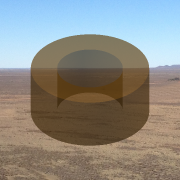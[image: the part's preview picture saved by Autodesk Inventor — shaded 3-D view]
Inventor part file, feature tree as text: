
AUTODESK INVENTOR PART (.ipt)
format: ipt  version: 2014 SP1 (Build 180222100, 222)  size: 130,048 bytes
history: native  units: in
note: dims shown in document units (in); Inventor stores cm internally (conversion verified against a paired STEP export)
features: extrude x1, sketch x1
ambient origin geometry x8: Origin, YZ Plane, XZ Plane, XY Plane, X Axis, Y Axis, Z Axis, Center Point
bodies: Solid1 (feature_tree)
feature tree (2):
  extrude  "Extrusion1"  Depth=4.0in
  sketch  "Sketch1"  dims[d0=9.0in d1=2.0in d2=4.0in d3=0.0in]
